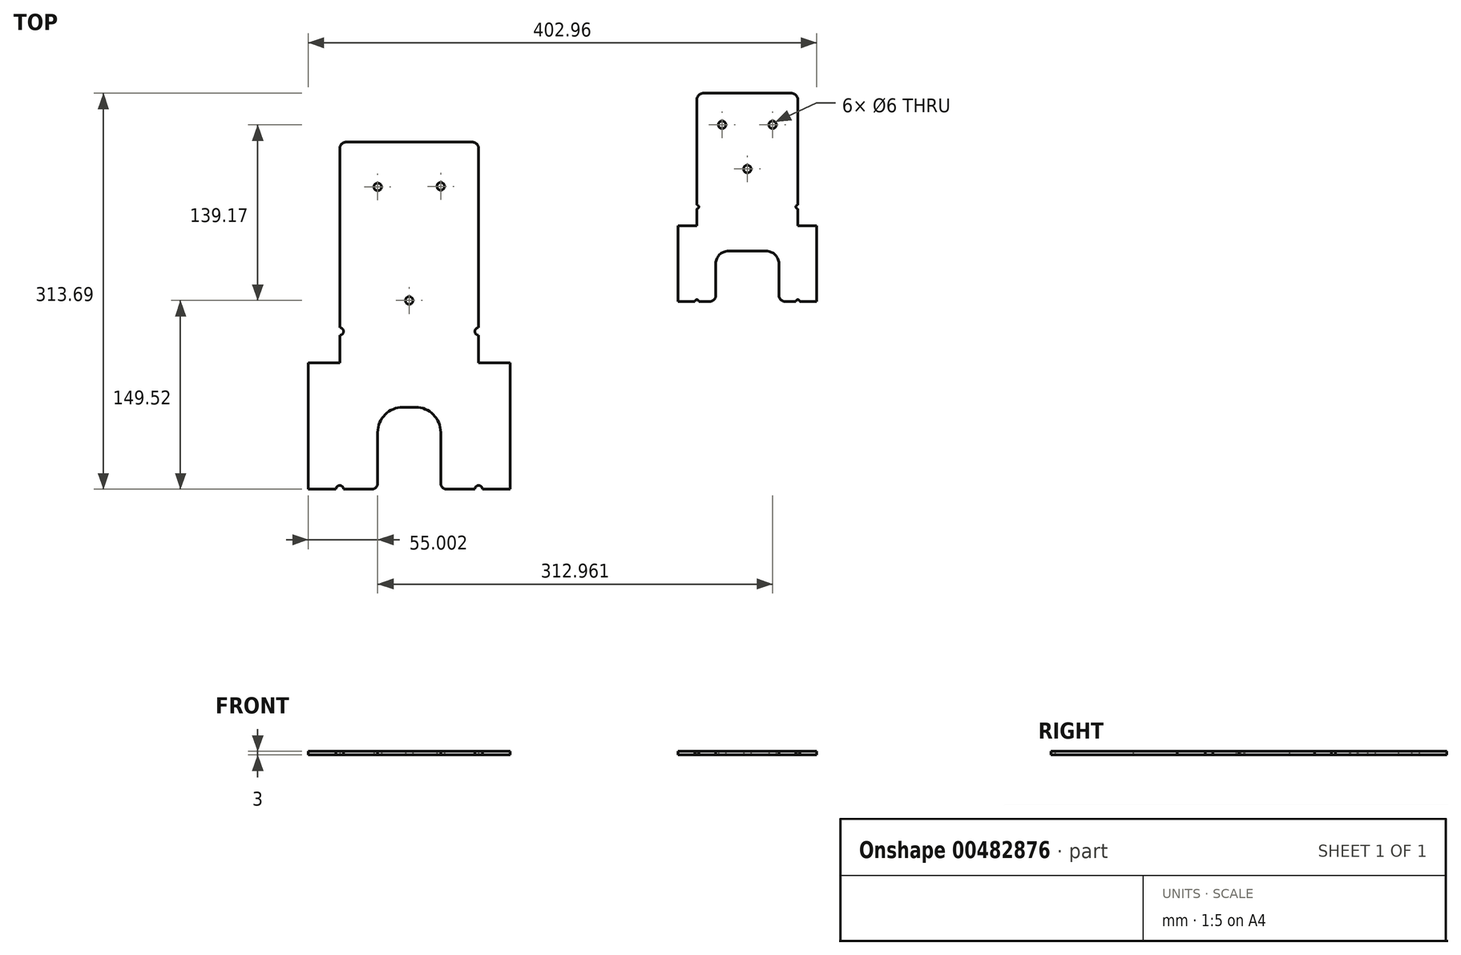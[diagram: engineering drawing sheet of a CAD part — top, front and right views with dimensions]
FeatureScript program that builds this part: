
annotation { "Feature Type Name" : "Feature", "Feature Type Description" : "" }
export const myFeature = defineFeature(function(context is Context, id is Id, definition is map)
    precondition{}
    {
        {
            var Q0;
            Q0=qCreatedBy(makeId("Top.planeOp"),FACE);
            var sketch = newSketch(context, id + "F0", { "sketchPlane" : qUnion([Q0])});
            skLineSegment(sketch, "E0", {"start": v(-61.3, 175.48) * mm, "end": v(38.7, 175.48) * mm});
            skLineSegment(sketch, "E1", {"start": v(43.7, 170.48) * mm, "end": v(43.7, 28.48) * mm});
            skLineSegment(sketch, "E2", {"start": v(40.7, -99.52) * mm, "end": v(18.7, -99.52) * mm});
            skLineSegment(sketch, "E3", {"start": v(-66.3, 0.48) * mm, "end": v(-66.3, 22.48) * mm});
            skLineSegment(sketch, "E4", {"start": v(46.7, -99.52) * mm, "end": v(68.7, -99.52) * mm});
            skLineSegment(sketch, "E5", {"start": v(68.7, -99.52) * mm, "end": v(68.7, 0.48) * mm});
            skLineSegment(sketch, "E6", {"start": v(68.7, 0.48) * mm, "end": v(43.7, 0.48) * mm});
            skLineSegment(sketch, "E7", {"start": v(-91.3, 0.48) * mm, "end": v(-91.3, -99.52) * mm});
            skLineSegment(sketch, "E8", {"start": v(-91.3, -99.52) * mm, "end": v(-69.3, -99.52) * mm});
            skLineSegment(sketch, "E9", {"start": v(-36.3, -94.52) * mm, "end": v(-36.3, -54.52) * mm});
            skLineSegment(sketch, "E10", {"start": v(-16.3, -34.52) * mm, "end": v(-6.3, -34.52) * mm});
            skLineSegment(sketch, "E11", {"start": v(13.7, -54.52) * mm, "end": v(13.7, -94.52) * mm});
            skLineSegment(sketch, "E12.trimOffspring", {"start": v(-41.3, -99.52) * mm, "end": v(-63.3, -99.52) * mm});
            skPoint(sketch, "E13.visualSharp", {"position": v(-36.3, -34.52) * mm});
            skArc(sketch, "E13.filletArc", {"start": v(-16.3, -34.52) * mm, "mid": v(-30.45, -40.38) * mm, "end": v(-36.3, -54.52) * mm});
            skPoint(sketch, "E14.visualSharp", {"position": v(13.7, -34.52) * mm});
            skArc(sketch, "E14.filletArc", {"start": v(13.7, -54.52) * mm, "mid": v(7.83, -40.38) * mm, "end": v(-6.3, -34.52) * mm});
            skPoint(sketch, "E15.visualSharp", {"position": v(-36.3, -99.52) * mm});
            skArc(sketch, "E15.filletArc", {"start": v(-41.3, -99.52) * mm, "mid": v(-37.77, -98.05) * mm, "end": v(-36.3, -94.52) * mm});
            skPoint(sketch, "E16.visualSharp", {"position": v(13.7, -99.52) * mm});
            skArc(sketch, "E16.filletArc", {"start": v(13.7, -94.52) * mm, "mid": v(15.16, -98.05) * mm, "end": v(18.7, -99.52) * mm});
            skPoint(sketch, "E17.visualSharp", {"position": v(-66.3, 175.48) * mm});
            skArc(sketch, "E17.filletArc", {"start": v(-61.3, 175.48) * mm, "mid": v(-64.84, 174.02) * mm, "end": v(-66.3, 170.48) * mm});
            skPoint(sketch, "E18.visualSharp", {"position": v(43.7, 175.48) * mm});
            skArc(sketch, "E18.filletArc", {"start": v(43.7, 170.48) * mm, "mid": v(42.23, 174.02) * mm, "end": v(38.7, 175.48) * mm});
            skArc(sketch, "E19", {"start": v(-66.3, 28.48) * mm, "mid": v(-63.3, 25.48) * mm, "end": v(-66.3, 22.48) * mm});
            skArc(sketch, "E20", {"start": v(43.7, 28.48) * mm, "mid": v(40.7, 25.48) * mm, "end": v(43.7, 22.48) * mm});
            skLineSegment(sketch, "E21.trimOffspring", {"start": v(-66.3, 28.48) * mm, "end": v(-66.3, 170.48) * mm});
            skLineSegment(sketch, "E22.trimOffspring", {"start": v(43.7, 22.48) * mm, "end": v(43.7, 0.48) * mm});
            skArc(sketch, "E23", {"start": v(46.7, -99.52) * mm, "mid": v(43.7, -96.52) * mm, "end": v(40.7, -99.52) * mm});
            skArc(sketch, "E24", {"start": v(-63.3, -99.52) * mm, "mid": v(-66.3, -96.52) * mm, "end": v(-69.3, -99.52) * mm});
            skLineSegment(sketch, "E25.trimOffspring", {"start": v(-66.3, 0.48) * mm, "end": v(-91.3, 0.48) * mm});
            skCircle(sketch, "E26", {"center": v(-11.3, 50) * mm, "radius": 3 * mm});
            skPoint(sketch, "E26.centerSnap0", {"position": v(-11.3, 175.48) * mm});
            skCircle(sketch, "E27", {"center": v(13.7, 140.48) * mm, "radius": 3 * mm});
            skCircle(sketch, "E28", {"center": v(-36.3, 140) * mm, "radius": 3 * mm});
            skSolve(sketch);
        }
        {
            var Q0;
            Q0 = qSketchRegion(id + "F0", true);
            extrude(context, id + "F1", {"entities" : qUnion([Q0]), "depth" : 3 * mm});
        }
        {
            var Q0;
            Q0=qCreatedBy(makeId("Top.planeOp"),FACE);
            var sketch = newSketch(context, id + "F2", { "sketchPlane" : qUnion([Q0])});
            skLineSegment(sketch, "E29", {"start": v(221.65, 214.17) * mm, "end": v(291.65, 214.17) * mm});
            skLineSegment(sketch, "E30", {"start": v(296.65, 209.17) * mm, "end": v(296.65, 125.67) * mm});
            skLineSegment(sketch, "E31", {"start": v(216.65, 109.17) * mm, "end": v(216.65, 122.67) * mm});
            skLineSegment(sketch, "E32", {"start": v(298.15, 49.17) * mm, "end": v(311.65, 49.17) * mm});
            skLineSegment(sketch, "E33", {"start": v(311.65, 49.17) * mm, "end": v(311.65, 109.17) * mm});
            skLineSegment(sketch, "E34", {"start": v(311.65, 109.17) * mm, "end": v(296.65, 109.17) * mm});
            skLineSegment(sketch, "E35", {"start": v(201.65, 109.17) * mm, "end": v(201.65, 49.17) * mm});
            skLineSegment(sketch, "E36", {"start": v(201.65, 49.17) * mm, "end": v(215.15, 49.17) * mm});
            skLineSegment(sketch, "E37.trimOffspring", {"start": v(226.68, 49.17) * mm, "end": v(218.15, 49.17) * mm});
            skPoint(sketch, "E38.visualSharp", {"position": v(231.65, 49.17) * mm});
            skArc(sketch, "E38.filletArc", {"start": v(226.68, 49.17) * mm, "mid": v(230.02, 50.44) * mm, "end": v(231.65, 53.62) * mm});
            skPoint(sketch, "E39.visualSharp", {"position": v(216.65, 214.17) * mm});
            skArc(sketch, "E39.filletArc", {"start": v(221.65, 214.17) * mm, "mid": v(218.12, 212.7) * mm, "end": v(216.65, 209.17) * mm});
            skPoint(sketch, "E40.visualSharp", {"position": v(296.65, 214.17) * mm});
            skArc(sketch, "E40.filletArc", {"start": v(296.65, 209.17) * mm, "mid": v(295.19, 212.7) * mm, "end": v(291.65, 214.17) * mm});
            skArc(sketch, "E41", {"start": v(216.65, 125.67) * mm, "mid": v(218.15, 124.17) * mm, "end": v(216.65, 122.67) * mm});
            skArc(sketch, "E42", {"start": v(296.65, 125.67) * mm, "mid": v(295.15, 124.17) * mm, "end": v(296.65, 122.67) * mm});
            skLineSegment(sketch, "E43.trimOffspring", {"start": v(216.65, 125.67) * mm, "end": v(216.65, 209.17) * mm});
            skLineSegment(sketch, "E44.trimOffspring", {"start": v(296.65, 122.67) * mm, "end": v(296.65, 109.17) * mm});
            skArc(sketch, "E45", {"start": v(298.15, 49.17) * mm, "mid": v(296.65, 50.67) * mm, "end": v(295.15, 49.17) * mm});
            skArc(sketch, "E46", {"start": v(218.15, 49.17) * mm, "mid": v(216.65, 50.67) * mm, "end": v(215.15, 49.17) * mm});
            skLineSegment(sketch, "E47.trimOffspring", {"start": v(216.65, 109.17) * mm, "end": v(201.65, 109.17) * mm});
            skLineSegment(sketch, "E48", {"start": v(216.65, 124.17) * mm, "end": v(296.65, 124.17) * mm, "construction": true});
            skLineSegment(sketch, "E49", {"start": v(216.65, 109.17) * mm, "end": v(296.65, 109.17) * mm, "construction": true});
            skLineSegment(sketch, "E50", {"start": v(231.65, 53.62) * mm, "end": v(231.65, 79.17) * mm});
            skLineSegment(sketch, "E51", {"start": v(281.65, 79.17) * mm, "end": v(281.65, 54.17) * mm});
            skLineSegment(sketch, "E52", {"start": v(295.15, 49.17) * mm, "end": v(286.65, 49.17) * mm});
            skPoint(sketch, "E53.visualSharp", {"position": v(281.65, 49.17) * mm});
            skArc(sketch, "E53.filletArc", {"start": v(281.65, 54.17) * mm, "mid": v(283.12, 50.64) * mm, "end": v(286.65, 49.17) * mm});
            skLineSegment(sketch, "E54", {"start": v(241.65, 89.17) * mm, "end": v(271.65, 89.17) * mm});
            skPoint(sketch, "E55.visualSharp", {"position": v(231.65, 89.17) * mm});
            skArc(sketch, "E55.filletArc", {"start": v(241.65, 89.17) * mm, "mid": v(234.58, 86.24) * mm, "end": v(231.65, 79.17) * mm});
            skPoint(sketch, "E56.visualSharp", {"position": v(281.65, 89.17) * mm});
            skArc(sketch, "E56.filletArc", {"start": v(281.65, 79.17) * mm, "mid": v(278.72, 86.24) * mm, "end": v(271.65, 89.17) * mm});
            skCircle(sketch, "E57", {"center": v(256.65, 154.17) * mm, "radius": 3 * mm});
            skPoint(sketch, "E57.centerSnap0", {"position": v(256.65, 124.17) * mm});
            skCircle(sketch, "E58", {"center": v(276.65, 189.17) * mm, "radius": 3 * mm});
            skCircle(sketch, "E59", {"center": v(236.65, 189.17) * mm, "radius": 3 * mm});
            skSolve(sketch);
        }
        {
            var Q0;
            Q0=makeQuery(id+"F2.imprint","IMPRINT",FACE,{"disambiguationData":[TD([[makeQuery(id+"F2.imprint","IMPRINT",EDGE,{"derivedFrom":sQuery(id+"F2.wireOp",EDGE,"E29")}),-1.0]])]});
            extrude(context, id + "F3", {"entities" : qUnion([Q0]), "depth" : 3 * mm});
        }
    });
